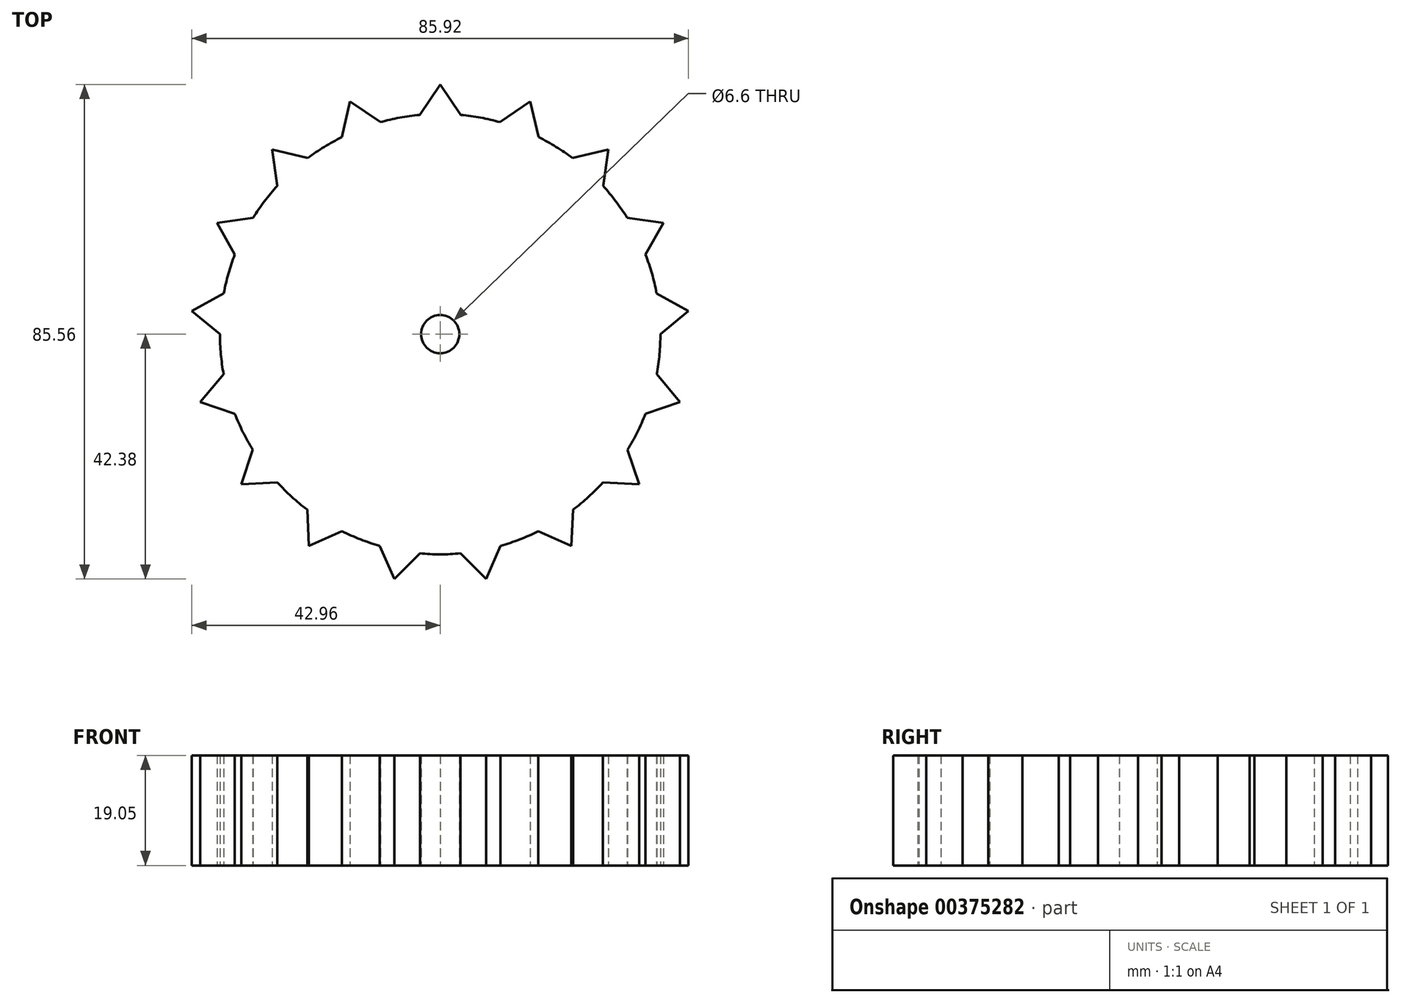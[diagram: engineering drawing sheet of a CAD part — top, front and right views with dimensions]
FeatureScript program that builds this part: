
annotation { "Feature Type Name" : "Feature", "Feature Type Description" : "" }
export const myFeature = defineFeature(function(context is Context, id is Id, definition is map)
    precondition{}
    {
        {
            var Q0;
            Q0=qCreatedBy(makeId("Top.planeOp"),FACE);
            var sketch = newSketch(context, id + "F0", { "sketchPlane" : qUnion([Q0])});
            skCircle(sketch, "E0", {"center": v(0, 0) * mm, "radius": 38.1 * mm});
            skLineSegment(sketch, "E1", {"start": v(0, 38.1) * mm, "end": v(0, 43.18) * mm});
            skLineSegment(sketch, "E2", {"start": v(0, 43.18) * mm, "end": v(-3.57, 37.93) * mm});
            skLineSegment(sketch, "E3", {"start": v(0, 43.18) * mm, "end": v(3.57, 37.93) * mm});
            skLineSegment(sketch, "E4.1.0", {"start": v(-15.59, 40.27) * mm, "end": v(-10.36, 36.66) * mm});
            skLineSegment(sketch, "E4.1.1", {"start": v(-15.59, 40.27) * mm, "end": v(-17.02, 34.08) * mm});
            skLineSegment(sketch, "E4.1.2", {"start": v(-13.75, 35.53) * mm, "end": v(-15.59, 40.27) * mm});
            skLineSegment(sketch, "E4.2.0", {"start": v(-29.07, 31.92) * mm, "end": v(-22.9, 30.45) * mm});
            skLineSegment(sketch, "E4.2.1", {"start": v(-29.07, 31.92) * mm, "end": v(-28.17, 25.63) * mm});
            skLineSegment(sketch, "E4.2.2", {"start": v(-25.65, 28.16) * mm, "end": v(-29.07, 31.92) * mm});
            skLineSegment(sketch, "E4.3.0", {"start": v(-38.62, 19.27) * mm, "end": v(-32.33, 20.13) * mm});
            skLineSegment(sketch, "E4.3.1", {"start": v(-38.62, 19.27) * mm, "end": v(-35.52, 13.73) * mm});
            skLineSegment(sketch, "E4.3.2", {"start": v(-34.08, 17) * mm, "end": v(-38.62, 19.27) * mm});
            skLineSegment(sketch, "E4.4.0", {"start": v(-42.96, 4.01) * mm, "end": v(-37.4, 7.09) * mm});
            skLineSegment(sketch, "E4.4.1", {"start": v(-42.96, 4.01) * mm, "end": v(-38.07, -0.03) * mm});
            skLineSegment(sketch, "E4.4.2", {"start": v(-37.9, 3.55) * mm, "end": v(-42.96, 4.01) * mm});
            skLineSegment(sketch, "E4.5.0", {"start": v(-41.5, -11.77) * mm, "end": v(-37.43, -6.9) * mm});
            skLineSegment(sketch, "E4.5.1", {"start": v(-41.5, -11.77) * mm, "end": v(-35.47, -13.78) * mm});
            skLineSegment(sketch, "E4.5.2", {"start": v(-36.61, -10.38) * mm, "end": v(-41.5, -11.77) * mm});
            skLineSegment(sketch, "E4.6.0", {"start": v(-34.43, -25.97) * mm, "end": v(-32.4, -19.95) * mm});
            skLineSegment(sketch, "E4.6.1", {"start": v(-34.43, -25.97) * mm, "end": v(-28.09, -25.66) * mm});
            skLineSegment(sketch, "E4.6.2", {"start": v(-30.38, -22.9) * mm, "end": v(-34.43, -25.97) * mm});
            skLineSegment(sketch, "E4.7.0", {"start": v(-22.71, -36.65) * mm, "end": v(-23, -30.3) * mm});
            skLineSegment(sketch, "E4.7.1", {"start": v(-22.71, -36.65) * mm, "end": v(-16.91, -34.07) * mm});
            skLineSegment(sketch, "E4.7.2", {"start": v(-20.04, -32.33) * mm, "end": v(-22.71, -36.65) * mm});
            skLineSegment(sketch, "E4.8.0", {"start": v(-7.93, -42.38) * mm, "end": v(-10.48, -36.56) * mm});
            skLineSegment(sketch, "E4.8.1", {"start": v(-7.93, -42.38) * mm, "end": v(-3.45, -37.88) * mm});
            skLineSegment(sketch, "E4.8.2", {"start": v(-7, -37.39) * mm, "end": v(-7.93, -42.38) * mm});
            skLineSegment(sketch, "E4.9.0", {"start": v(7.93, -42.38) * mm, "end": v(3.45, -37.88) * mm});
            skLineSegment(sketch, "E4.9.1", {"start": v(7.93, -42.38) * mm, "end": v(10.48, -36.56) * mm});
            skLineSegment(sketch, "E4.9.2", {"start": v(7, -37.39) * mm, "end": v(7.93, -42.38) * mm});
            skLineSegment(sketch, "E4.10.0", {"start": v(22.71, -36.65) * mm, "end": v(16.91, -34.07) * mm});
            skLineSegment(sketch, "E4.10.1", {"start": v(22.71, -36.65) * mm, "end": v(23, -30.3) * mm});
            skLineSegment(sketch, "E4.10.2", {"start": v(20.04, -32.33) * mm, "end": v(22.71, -36.65) * mm});
            skLineSegment(sketch, "E4.11.0", {"start": v(34.43, -25.97) * mm, "end": v(28.09, -25.66) * mm});
            skLineSegment(sketch, "E4.11.1", {"start": v(34.43, -25.97) * mm, "end": v(32.4, -19.95) * mm});
            skLineSegment(sketch, "E4.11.2", {"start": v(30.38, -22.9) * mm, "end": v(34.43, -25.97) * mm});
            skLineSegment(sketch, "E4.12.0", {"start": v(41.5, -11.77) * mm, "end": v(35.47, -13.78) * mm});
            skLineSegment(sketch, "E4.12.1", {"start": v(41.5, -11.77) * mm, "end": v(37.43, -6.9) * mm});
            skLineSegment(sketch, "E4.12.2", {"start": v(36.61, -10.38) * mm, "end": v(41.5, -11.77) * mm});
            skLineSegment(sketch, "E4.13.0", {"start": v(42.96, 4.01) * mm, "end": v(38.07, -0.03) * mm});
            skLineSegment(sketch, "E4.13.1", {"start": v(42.96, 4.01) * mm, "end": v(37.4, 7.09) * mm});
            skLineSegment(sketch, "E4.13.2", {"start": v(37.9, 3.55) * mm, "end": v(42.96, 4.01) * mm});
            skLineSegment(sketch, "E4.14.0", {"start": v(38.62, 19.27) * mm, "end": v(35.52, 13.73) * mm});
            skLineSegment(sketch, "E4.14.1", {"start": v(38.62, 19.27) * mm, "end": v(32.33, 20.13) * mm});
            skLineSegment(sketch, "E4.14.2", {"start": v(34.08, 17) * mm, "end": v(38.62, 19.27) * mm});
            skLineSegment(sketch, "E4.15.0", {"start": v(29.07, 31.92) * mm, "end": v(28.17, 25.63) * mm});
            skLineSegment(sketch, "E4.15.1", {"start": v(29.07, 31.92) * mm, "end": v(22.9, 30.45) * mm});
            skLineSegment(sketch, "E4.15.2", {"start": v(25.65, 28.16) * mm, "end": v(29.07, 31.92) * mm});
            skLineSegment(sketch, "E4.16.0", {"start": v(15.59, 40.27) * mm, "end": v(17.02, 34.08) * mm});
            skLineSegment(sketch, "E4.16.1", {"start": v(15.59, 40.27) * mm, "end": v(10.36, 36.66) * mm});
            skLineSegment(sketch, "E4.16.2", {"start": v(13.75, 35.53) * mm, "end": v(15.59, 40.27) * mm});
            skPoint(sketch, "E4.center", {"position": v(0, 0.03) * mm});
            skCircle(sketch, "E5", {"center": v(0, 0) * mm, "radius": 3.3 * mm});
            skSolve(sketch);
        }
        {
            var Q0;
            Q0 = qSketchRegion(id + "F0", true);
            extrude(context, id + "F1", {"entities" : qUnion([Q0]), "depth" : 19.05 * mm});
        }
    });
